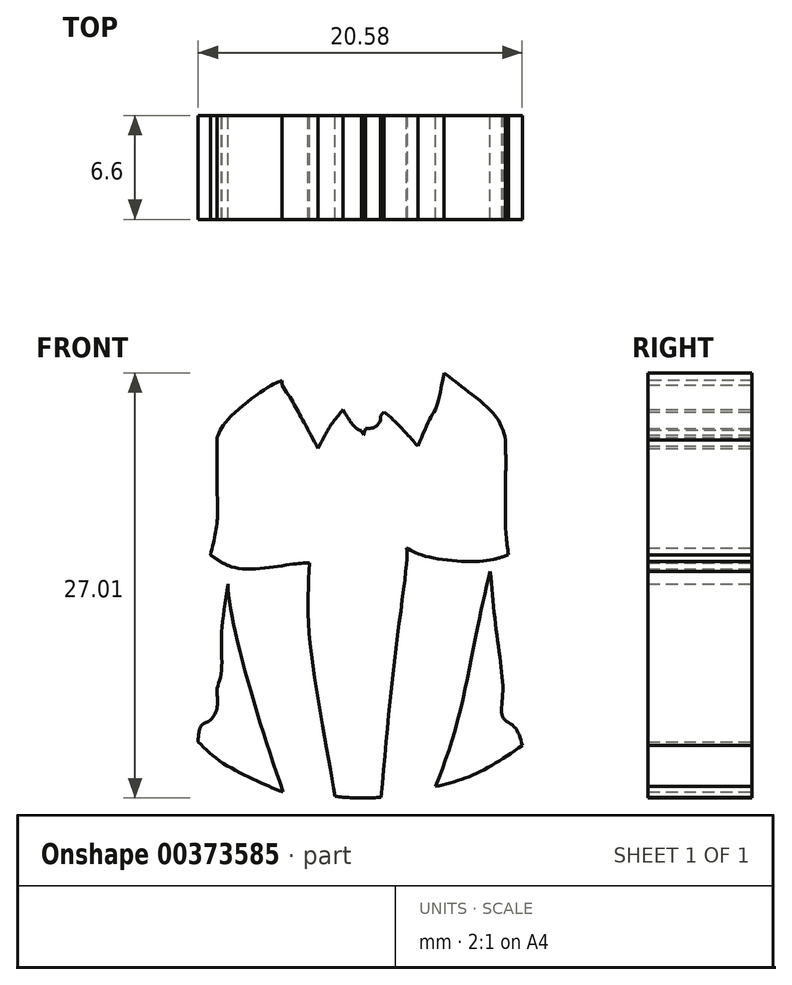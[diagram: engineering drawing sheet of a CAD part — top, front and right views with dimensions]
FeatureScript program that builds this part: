
annotation { "Feature Type Name" : "Feature", "Feature Type Description" : "" }
export const myFeature = defineFeature(function(context is Context, id is Id, definition is map)
    precondition{}
    {
        {
            var Q0;
            Q0=qCreatedBy(makeId("Front.planeOp"),FACE);
            var sketch = newSketch(context, id + "F0", { "sketchPlane" : qUnion([Q0])});
            skFitSpline(sketch, "E0", {"points": [v(-35.78, 54.46) * mm, v(-33.09, 59.85) * mm, v(-24.77, 66.06) * mm, v(-13.06, 67.81) * mm, v(-3.45, 65.7) * mm, v(-1.58, 65.82) * mm], "startDerivative": vector(10.86, 29.93) * mm, "endDerivative": vector(15.04, 3.36) * mm});
            skFitSpline(sketch, "E1", {"points": [v(-6.38, 64.18) * mm, v(-3.34, 64.3) * mm, v(-1.58, 65.82) * mm], "startDerivative": vector(6.22, -0.6) * mm, "endDerivative": vector(3.32, 3.98) * mm});
            skFitSpline(sketch, "E2", {"points": [v(-6.38, 64.18) * mm, v(-1.58, 62.66) * mm, v(2.4, 58.56) * mm, v(3.93, 55.63) * mm], "startDerivative": vector(14.2, -2.58) * mm, "endDerivative": vector(4.35, -9.84) * mm});
            skFitSpline(sketch, "E3", {"points": [v(3.93, 55.63) * mm, v(6.86, 54.23) * mm, v(8.96, 54.34) * mm], "startDerivative": vector(5.45, -3.31) * mm, "endDerivative": vector(4.6, 0.89) * mm});
            skFitSpline(sketch, "E4", {"points": [v(3.93, 54.21) * mm, v(5.68, 52.47) * mm, v(8.96, 54.34) * mm], "startDerivative": vector(3.48, -5.52) * mm, "endDerivative": vector(6.49, 5.4) * mm});
            skFitSpline(sketch, "E5", {"points": [v(5.68, 52.47) * mm, v(6.86, 48.72) * mm, v(6.86, 43.1) * mm, v(5.68, 41.7) * mm], "startDerivative": vector(3.82, -9.5) * mm, "endDerivative": vector(-5.74, -4.27) * mm});
            skFitSpline(sketch, "E6", {"points": [v(0, 51.42) * mm, v(1.35, 47.78) * mm, v(1.35, 45.1) * mm], "startDerivative": vector(3.15, -6.86) * mm, "endDerivative": vector(-0.56, -5.76) * mm});
            skFitSpline(sketch, "E7", {"points": [v(0, 51.42) * mm, v(3.93, 47.78) * mm, v(4.93, 43.33) * mm, v(5.68, 41.7) * mm], "startDerivative": vector(11.87, -7.83) * mm, "endDerivative": vector(3.7, -5.88) * mm});
            skFitSpline(sketch, "E8", {"points": [v(-7.7, 51.06) * mm, v(-5.13, 50.09) * mm, v(-0.67, 47.3) * mm, v(1.35, 45.1) * mm], "startDerivative": vector(8.03, -2.55) * mm, "endDerivative": vector(5.45, -7.1) * mm});
            skFitSpline(sketch, "E9", {"points": [v(-7.7, 51.06) * mm, v(-5.83, 48.77) * mm, v(-1.79, 45.96) * mm], "startDerivative": vector(3.67, -5.32) * mm, "endDerivative": vector(7.99, -4.9) * mm});
            skFitSpline(sketch, "E10", {"points": [v(-1.79, 45.96) * mm, v(-4.78, 45.96) * mm, v(-11.33, 49.25) * mm, v(-14.95, 51.76) * mm], "startDerivative": vector(-10.08, -1.7) * mm, "endDerivative": vector(-9.87, 7.2) * mm});
            skFitSpline(sketch, "E11", {"points": [v(-11.68, 45.1) * mm, v(-12.44, 48.14) * mm, v(-14.95, 51.76) * mm], "startDerivative": vector(-1, 6.65) * mm, "endDerivative": vector(-5.43, 6.69) * mm});
            skFitSpline(sketch, "E12", {"points": [v(-11.68, 45.1) * mm, v(-13.97, 47.7) * mm, v(-19.5, 51.76) * mm], "startDerivative": vector(-4.7, 6.12) * mm, "endDerivative": vector(-10.62, 7.16) * mm});
            skFitSpline(sketch, "E13", {"points": [v(-18.62, 45.1) * mm, v(-18.62, 48.14) * mm, v(-19.5, 51.76) * mm], "startDerivative": vector(0.4, 6.3) * mm, "endDerivative": vector(-2.13, 7.02) * mm});
            skFitSpline(sketch, "E14", {"points": [v(-20.14, 48.19) * mm, v(-19.3, 46.86) * mm, v(-18.62, 45.1) * mm], "startDerivative": vector(1.86, -2.65) * mm, "endDerivative": vector(1.2, -3.53) * mm});
            skFitSpline(sketch, "E15", {"points": [v(-22.6, 48.73) * mm, v(-20.78, 46.96) * mm, v(-19.55, 45.1) * mm], "startDerivative": vector(3.79, -3.33) * mm, "endDerivative": vector(2.3, -3.96) * mm});
            skFitSpline(sketch, "E16", {"points": [v(-20.14, 48.19) * mm, v(-19.3, 45.7) * mm, v(-19.55, 45.1) * mm], "startDerivative": vector(1.92, -4.36) * mm, "endDerivative": vector(-1.07, -1.52) * mm});
            skFitSpline(sketch, "E17", {"points": [v(-25.36, 50.22) * mm, v(-25.4, 46.4) * mm], "startDerivative": vector(-0.03, -3.81) * mm, "endDerivative": vector(-0.03, -3.81) * mm});
            skFitSpline(sketch, "E18", {"points": [v(-28.3, 48.16) * mm, v(-26.94, 47.5) * mm, v(-25.4, 46.4) * mm], "startDerivative": vector(2.87, -1.25) * mm, "endDerivative": vector(2.94, -2.24) * mm});
            skFitSpline(sketch, "E19", {"points": [v(-25.39, 47.04) * mm, v(-24.28, 48.16) * mm, v(-22.6, 48.73) * mm], "startDerivative": vector(2.06, 2.6) * mm, "endDerivative": vector(3.5, 0.8) * mm});
            skFitSpline(sketch, "E20", {"points": [v(-28.3, 48.16) * mm, v(-28.83, 43.89) * mm, v(-28.83, 43.03) * mm, v(-27.85, 38.2) * mm, v(-26.6, 36.06) * mm], "startDerivative": vector(-2.2, -17.32) * mm, "endDerivative": vector(5.7, -7.14) * mm});
            skFitSpline(sketch, "E21", {"points": [v(-28.3, 36.87) * mm, v(-27.46, 36.27) * mm, v(-26.6, 36.06) * mm], "startDerivative": vector(1.58, -1.34) * mm, "endDerivative": vector(1.82, -0.28) * mm});
            skFitSpline(sketch, "E22", {"points": [v(-30.88, 38.2) * mm, v(-29.25, 36.06) * mm, v(-27.37, 34.56) * mm], "startDerivative": vector(2.98, -4.44) * mm, "endDerivative": vector(4.04, -2.82) * mm});
            skFitSpline(sketch, "E23", {"points": [v(-28.3, 36.87) * mm, v(-27.85, 35.67) * mm, v(-27.37, 34.56) * mm], "startDerivative": vector(0.87, -2.39) * mm, "endDerivative": vector(0.98, -2.23) * mm});
            skFitSpline(sketch, "E24", {"points": [v(-30.88, 38.2) * mm, v(-30.28, 36.06) * mm, v(-28.3, 32.93) * mm], "startDerivative": vector(0.9, -4.76) * mm, "endDerivative": vector(4.12, -5.72) * mm});
            skFitSpline(sketch, "E25", {"points": [v(-30.88, 34.9) * mm, v(-29.77, 33.7) * mm, v(-28.3, 32.93) * mm], "startDerivative": vector(2.06, -2.62) * mm, "endDerivative": vector(3.1, -1.32) * mm});
            skFitSpline(sketch, "E26", {"points": [v(-30.88, 34.9) * mm, v(-30.26, 33.7) * mm, v(-29.1, 32.32) * mm], "startDerivative": vector(1.16, -2.58) * mm, "endDerivative": vector(2.37, -2.57) * mm});
            skFitSpline(sketch, "E27", {"points": [v(-31.59, 34.01) * mm, v(-30.54, 32.93) * mm, v(-29.1, 32.32) * mm], "startDerivative": vector(1.94, -2.42) * mm, "endDerivative": vector(3.02, -0.96) * mm});
            skFitSpline(sketch, "E28", {"points": [v(-31.59, 34.01) * mm, v(-30.88, 32.04) * mm, v(-29.47, 29.77) * mm, v(-27.85, 28.08) * mm], "startDerivative": vector(1.88, -6.17) * mm, "endDerivative": vector(5, -4.76) * mm});
            skFitSpline(sketch, "E29", {"points": [v(-32.7, 30.62) * mm, v(-31.27, 29.23) * mm, v(-29.1, 28.02) * mm, v(-27.85, 28.08) * mm], "startDerivative": vector(3.73, -4.02) * mm, "endDerivative": vector(4.29, 0.93) * mm});
            skFitSpline(sketch, "E30", {"points": [v(-32.7, 30.62) * mm, v(-33.17, 28.08) * mm, v(-32.15, 25.21) * mm, v(-29.1, 23.2) * mm, v(-27.37, 22.4) * mm], "startDerivative": vector(-2.96, -10.2) * mm, "endDerivative": vector(7.48, -3.45) * mm});
            skFitSpline(sketch, "E31", {"points": [v(-39.04, 37.32) * mm, v(-39.3, 32.93) * mm, v(-37.7, 28.98) * mm, v(-35.36, 26.2) * mm, v(-32.4, 23.59) * mm, v(-27.37, 22.4) * mm], "startDerivative": vector(-3.4, -21.75) * mm, "endDerivative": vector(24.84, -3.15) * mm});
            skFitSpline(sketch, "E32", {"points": [v(-39.04, 37.32) * mm, v(-39.93, 34.9) * mm, v(-41.09, 32.93) * mm], "startDerivative": vector(-1.58, -4.86) * mm, "endDerivative": vector(-2.54, -3.9) * mm});
            skFitSpline(sketch, "E33", {"points": [v(-35.78, 54.46) * mm, v(-39.04, 51.7) * mm, v(-41.02, 45.3) * mm, v(-41.02, 38.2) * mm, v(-41.09, 32.93) * mm], "startDerivative": vector(-16.55, -10.36) * mm, "endDerivative": vector(-0.72, -21.25) * mm});
            skFitSpline(sketch, "E34", {"points": [v(5.68, 41.7) * mm, v(6.42, 38.2) * mm, v(8.99, 34.9) * mm], "startDerivative": vector(0.72, -7.5) * mm, "endDerivative": vector(5.83, -6.1) * mm});
            skFitSpline(sketch, "E35", {"points": [v(8.99, 34.9) * mm, v(8.13, 34.01) * mm], "startDerivative": vector(-0.86, -0.89) * mm, "endDerivative": vector(-0.86, -0.89) * mm});
            skFitSpline(sketch, "E36", {"points": [v(-27.37, 22.4) * mm, v(-25.36, 20.57) * mm, v(-22.6, 19.8) * mm], "startDerivative": vector(3.73, -4.24) * mm, "endDerivative": vector(5.8, -0.97) * mm});
            skFitSpline(sketch, "E37", {"points": [v(-22.6, 19.8) * mm, v(-21.84, 21.8) * mm, v(-19.9, 24.77) * mm, v(-19.6, 23.8) * mm], "startDerivative": vector(1.48, 4.88) * mm, "endDerivative": vector(0.58, -6.35) * mm});
            skFitSpline(sketch, "E38", {"points": [v(-19.6, 23.8) * mm, v(-17.55, 26.1) * mm, v(-16.52, 25.98) * mm], "startDerivative": vector(3.39, 4.89) * mm, "endDerivative": vector(2.72, -1.06) * mm});
            skFitSpline(sketch, "E39", {"points": [v(-17.85, 23.8) * mm, v(-16.52, 25.98) * mm], "startDerivative": vector(1.33, 2.18) * mm, "endDerivative": vector(1.33, 2.18) * mm});
            skFitSpline(sketch, "E40", {"points": [v(-17.85, 23.8) * mm, v(-16.52, 24.3) * mm, v(-14.58, 24.3) * mm], "startDerivative": vector(2.72, 1.3) * mm, "endDerivative": vector(3.78, -0.29) * mm});
            skFitSpline(sketch, "E41", {"points": [v(-16.52, 22.4) * mm, v(-15.5, 23.24) * mm, v(-14.58, 24.3) * mm], "startDerivative": vector(2.13, 1.62) * mm, "endDerivative": vector(1.74, 2.17) * mm});
            skFitSpline(sketch, "E42", {"points": [v(-16.21, 20.46) * mm, v(-15.04, 21.35) * mm, v(-13.87, 22.8) * mm, v(-13.8, 23.8) * mm], "startDerivative": vector(3.34, 2.31) * mm, "endDerivative": vector(-0.34, 3.44) * mm});
            skFitSpline(sketch, "E43", {"points": [v(-16.52, 22.4) * mm, v(-15.73, 22.4) * mm, v(-14.58, 23.34) * mm, v(-14.38, 23.8) * mm, v(-13.8, 23.8) * mm], "startDerivative": vector(2.93, -0.64) * mm, "endDerivative": vector(3.34, -0.57) * mm});
            skFitSpline(sketch, "E44", {"points": [v(-19.6, 14.98) * mm, v(-18.89, 16.78) * mm, v(-16.52, 18.65) * mm, v(-14.58, 19.8) * mm, v(-14.58, 20.74) * mm, v(-16.21, 20.46) * mm], "startDerivative": vector(2.25, 9.04) * mm, "endDerivative": vector(-10.8, -4.04) * mm});
            skFitSpline(sketch, "E45", {"points": [v(-22.6, 19.8) * mm, v(-22.6, 18.51) * mm, v(-24.71, 14.98) * mm, v(-26.6, 12.03) * mm, v(-26.6, 10.16) * mm, v(-25.36, 7.7) * mm, v(-21.84, 8.1) * mm, v(-20.6, 12.48) * mm, v(-19.6, 14.98) * mm], "startDerivative": vector(2.63, -13.87) * mm, "endDerivative": vector(9.82, 18.02) * mm});
            skFitSpline(sketch, "E46", {"points": [v(-13.8, 37.83) * mm, v(-16.21, 38.2) * mm, v(-19.35, 38) * mm, v(-21.24, 37.1) * mm, v(-23.55, 35.39) * mm, v(-24.34, 34.01) * mm], "startDerivative": vector(-11.21, 2.22) * mm, "endDerivative": vector(-3.42, -8.47) * mm});
            skFitSpline(sketch, "E47", {"points": [v(-24.34, 34.01) * mm, v(-23.68, 33.33) * mm, v(-23.2, 32.93) * mm], "startDerivative": vector(1.23, -1.34) * mm, "endDerivative": vector(1.03, -0.8) * mm});
            skFitSpline(sketch, "E48", {"points": [v(-13.8, 37.83) * mm, v(-13.43, 37.6) * mm], "startDerivative": vector(0.37, -0.23) * mm, "endDerivative": vector(0.37, -0.23) * mm});
            skFitSpline(sketch, "E49", {"points": [v(-23.2, 32.93) * mm, v(-22.84, 33.82) * mm, v(-21.55, 35.3) * mm, v(-18.85, 36.72) * mm, v(-17.55, 37.26) * mm, v(-14.32, 37.51) * mm, v(-13.43, 37.6) * mm], "startDerivative": vector(2.32, 7) * mm, "endDerivative": vector(5.9, 0.82) * mm});
            skFitSpline(sketch, "E50", {"points": [v(-23.2, 32.93) * mm, v(-22.16, 32.07) * mm, v(-20.07, 31.13) * mm, v(-17.58, 31.02) * mm, v(-13.18, 32.93) * mm], "startDerivative": vector(5.1, -4.84) * mm, "endDerivative": vector(13.78, 7.2) * mm});
            skFitSpline(sketch, "E51", {"points": [v(-13.18, 32.93) * mm, v(-12.97, 34.38) * mm, v(-13.18, 36.06) * mm, v(-13.43, 37.05) * mm, v(-13.73, 37.56) * mm], "startDerivative": vector(1.07, 4.96) * mm, "endDerivative": vector(-1.82, 2.61) * mm});
            skFitSpline(sketch, "E52", {"points": [v(-16.59, 31.32) * mm, v(-17.53, 31.95) * mm, v(-18.37, 33.45) * mm, v(-18.45, 35.12) * mm, v(-17.58, 36.38) * mm, v(-16.01, 36.66) * mm, v(-14.94, 36.4) * mm, v(-14.2, 35.1) * mm, v(-14.22, 32.93) * mm, v(-14.33, 32.34) * mm], "startDerivative": vector(-9.83, 5) * mm, "endDerivative": vector(-1.64, -6.43) * mm});
            skFitSpline(sketch, "E53", {"points": [v(-17.58, 34.3) * mm, v(-17.55, 33.82) * mm, v(-17.21, 33.22) * mm, v(-16.8, 33.82) * mm, v(-16.46, 34.13) * mm, v(-16.42, 35.27) * mm, v(-16.8, 35.7) * mm, v(-17.55, 35.46) * mm, v(-17.79, 34.9) * mm, v(-17.75, 34.54) * mm, v(-17.58, 34.3) * mm]});
            skFitSpline(sketch, "E54", {"points": [v(-14.94, 34.22) * mm, v(-14.62, 34.17) * mm, v(-14.56, 33.22) * mm, v(-15, 33.22) * mm, v(-15.46, 33.22) * mm, v(-15.78, 33.22) * mm, v(-16, 33.45) * mm, v(-15.29, 33.53) * mm, v(-14.99, 33.82) * mm, v(-14.94, 34.22) * mm]});
            skFitSpline(sketch, "E55", {"points": [v(-21.86, 40.58) * mm, v(-20.54, 42) * mm, v(-19.37, 43) * mm, v(-17.81, 43.17) * mm, v(-17.4, 42.76) * mm, v(-17.79, 42.15) * mm, v(-19.19, 41.75) * mm, v(-20.51, 41.11) * mm, v(-21.86, 40.58) * mm]});
            skFitSpline(sketch, "E56", {"points": [v(-30.97, 28.2) * mm, v(-31.3, 28.04) * mm, v(-31.35, 27.36) * mm, v(-31.27, 26.59) * mm, v(-30.7, 25.8) * mm, v(-29.36, 25) * mm, v(-29.04, 24.94) * mm, v(-29.2, 25.39) * mm, v(-29.7, 25.86) * mm, v(-30.46, 26.52) * mm, v(-30.7, 26.9) * mm, v(-30.82, 27.76) * mm, v(-30.97, 28.2) * mm]});
            skFitSpline(sketch, "E57", {"points": [v(-28.79, 44.25) * mm, v(-27.31, 45.49) * mm, v(-25.77, 46.69) * mm], "startDerivative": vector(2.92, 2.5) * mm, "endDerivative": vector(3.1, 2.35) * mm});
            skFitSpline(sketch, "E58", {"points": [v(-23.28, 7.38) * mm, v(-23.34, 3.18) * mm, v(-22.86, 0) * mm, v(-22.26, -2.26) * mm, v(-22.26, -4.08) * mm, v(-21.65, -3.47) * mm, v(-20.8, -2.26) * mm], "startDerivative": vector(-0.82, -18.5) * mm, "endDerivative": vector(5.85, 8.57) * mm});
            skFitSpline(sketch, "E59", {"points": [v(-20.8, -2.26) * mm, v(-19.94, -4.93) * mm, v(-18.82, -7.88) * mm], "startDerivative": vector(1.69, -5.44) * mm, "endDerivative": vector(2.28, -5.8) * mm});
            skFitSpline(sketch, "E60", {"points": [v(-18.82, -7.88) * mm, v(-18.2, -6.6) * mm, v(-18, -5.44) * mm], "startDerivative": vector(1.37, 2.44) * mm, "endDerivative": vector(0.25, 2.45) * mm});
            skFitSpline(sketch, "E61", {"points": [v(-18, -5.44) * mm, v(-16.63, -7.12) * mm, v(-15.87, -7.32) * mm], "startDerivative": vector(2.26, -3.36) * mm, "endDerivative": vector(2, -0.14) * mm});
            skFitSpline(sketch, "E62", {"points": [v(-17.14, -1.42) * mm, v(-16.38, -3.5) * mm, v(-15.87, -7.32) * mm], "startDerivative": vector(1.96, -4.43) * mm, "endDerivative": vector(0.65, -7.25) * mm});
            skFitSpline(sketch, "E63", {"points": [v(-17.14, -1.42) * mm, v(-15.87, -2.06) * mm], "startDerivative": vector(1.27, -0.64) * mm, "endDerivative": vector(1.27, -0.64) * mm});
            skFitSpline(sketch, "E64", {"points": [v(-14.4, 8.3) * mm, v(-15.2, 6.36) * mm, v(-15.87, 3.77) * mm, v(-15.87, 0) * mm, v(-15.87, -2.06) * mm], "startDerivative": vector(-3.72, -8.42) * mm, "endDerivative": vector(-0.16, -8.38) * mm});
            skFitSpline(sketch, "E65", {"points": [v(-14.4, 8.3) * mm, v(-13.73, 6.87) * mm, v(-13.68, 3.62) * mm], "startDerivative": vector(1.93, -3.06) * mm, "endDerivative": vector(-0.36, -6.12) * mm});
            skFitSpline(sketch, "E66", {"points": [v(-9.36, 12.16) * mm, v(-9.97, 9.37) * mm, v(-11.09, 6.36) * mm, v(-13.68, 3.62) * mm], "startDerivative": vector(-1.82, -8.85) * mm, "endDerivative": vector(-8.2, -7.26) * mm});
            skFitSpline(sketch, "E67", {"points": [v(-9.36, 12.16) * mm, v(-8.44, 9.15) * mm, v(-6.35, 5.84) * mm, v(-5.23, 4.47) * mm], "startDerivative": vector(1.84, -8.43) * mm, "endDerivative": vector(3.88, -4.54) * mm});
            skFitSpline(sketch, "E68", {"points": [v(-5.23, 8.3) * mm, v(-5.23, 4.47) * mm], "startDerivative": vector(0, -3.83) * mm, "endDerivative": vector(0, -3.83) * mm});
            skFitSpline(sketch, "E69", {"points": [v(-5.23, 8.3) * mm, v(-2.64, 6.14) * mm, v(0, 4.47) * mm], "startDerivative": vector(5.02, -4.43) * mm, "endDerivative": vector(5.45, -3.23) * mm});
            skFitSpline(sketch, "E70", {"points": [v(-0.65, 6.2) * mm, v(0, 5.43) * mm, v(0, 4.47) * mm], "startDerivative": vector(1.62, -1.4) * mm, "endDerivative": vector(-0.32, -2.06) * mm});
            skFitSpline(sketch, "E71", {"points": [v(0, 5.43) * mm, v(0.87, 4.47) * mm, v(1.84, 2.89) * mm], "startDerivative": vector(1.94, -1.94) * mm, "endDerivative": vector(1.74, -3.11) * mm});
            skFitSpline(sketch, "E72", {"points": [v(0.77, 8.38) * mm, v(1.53, 6.6) * mm, v(1.94, 4.47) * mm, v(1.84, 2.89) * mm], "startDerivative": vector(2.45, -5.04) * mm, "endDerivative": vector(-0.63, -4.93) * mm});
            skFitSpline(sketch, "E73", {"points": [v(0.77, 8.38) * mm, v(3.16, 6.35) * mm, v(8.35, 3.5) * mm, v(10.23, 2.89) * mm], "startDerivative": vector(6.23, -6.11) * mm, "endDerivative": vector(6.35, -1.6) * mm});
            skFitSpline(sketch, "E74", {"points": [v(8.4, 5.43) * mm, v(9.47, 4.47) * mm, v(10.23, 2.89) * mm], "startDerivative": vector(2.43, -1.8) * mm, "endDerivative": vector(1.25, -3.26) * mm});
            skFitSpline(sketch, "E75", {"points": [v(9.47, 4.47) * mm, v(11.3, 3.17) * mm, v(14.43, 1.5) * mm, v(17.76, 0.9) * mm], "startDerivative": vector(5.9, -4.32) * mm, "endDerivative": vector(9.5, -0.91) * mm});
            skFitSpline(sketch, "E76", {"points": [v(17.76, 0.9) * mm, v(18.62, -1.15) * mm, v(18.96, -4.2) * mm, v(18.83, -4.8) * mm], "startDerivative": vector(2.57, -4.83) * mm, "endDerivative": vector(-0.84, -2.34) * mm});
            skFitSpline(sketch, "E77", {"points": [v(20.29, -1.88) * mm, v(20.25, -3.6) * mm, v(18.89, -4.64) * mm], "startDerivative": vector(0.57, -3.76) * mm, "endDerivative": vector(-3.37, -1.76) * mm});
            skFitSpline(sketch, "E78", {"points": [v(20.25, -3.6) * mm, v(19.66, -5.87) * mm, v(18.54, -8.86) * mm], "startDerivative": vector(-1.1, -4.78) * mm, "endDerivative": vector(-2.28, -5.73) * mm});
            skFitSpline(sketch, "E79", {"points": [v(18.54, -8.86) * mm, v(20.25, -7.54) * mm, v(21.54, -5.65) * mm], "startDerivative": vector(3.67, 2.44) * mm, "endDerivative": vector(2.32, 3.97) * mm});
            skFitSpline(sketch, "E80", {"points": [v(20.25, -8.86) * mm, v(21.11, -7.37) * mm, v(21.54, -5.65) * mm], "startDerivative": vector(1.96, 2.91) * mm, "endDerivative": vector(0.63, 3.5) * mm});
            skFitSpline(sketch, "E81", {"points": [v(20.25, -8.86) * mm, v(21.54, -7.7) * mm, v(22.57, -4.64) * mm], "startDerivative": vector(3.33, 2.19) * mm, "endDerivative": vector(1.4, 6.06) * mm});
            skFitSpline(sketch, "E82", {"points": [v(26.04, 4.47) * mm, v(25.9, 1.67) * mm, v(24.3, -2.57) * mm, v(22.57, -4.64) * mm], "startDerivative": vector(0.27, -8.4) * mm, "endDerivative": vector(-5.95, -5.77) * mm});
            skFitSpline(sketch, "E83", {"points": [v(20.25, 23.62) * mm, v(23.8, 18.8) * mm, v(26.54, 12.9) * mm, v(27.62, 7.28) * mm, v(26.04, 4.47) * mm], "startDerivative": vector(14.13, -17.43) * mm, "endDerivative": vector(-10.63, -12.77) * mm});
            skFitSpline(sketch, "E84", {"points": [v(10.72, 30.44) * mm, v(14.03, 28.92) * mm, v(20.25, 23.62) * mm], "startDerivative": vector(7.85, -2.76) * mm, "endDerivative": vector(10.99, -10.37) * mm});
            skFitSpline(sketch, "E85", {"points": [v(-18.43, -7.16) * mm, v(-17.63, -8.03) * mm, v(-16.42, -9) * mm], "startDerivative": vector(1.6, -1.88) * mm, "endDerivative": vector(2.41, -1.8) * mm});
            skFitSpline(sketch, "E86", {"points": [v(-16.42, -9) * mm, v(-16.15, -11.08) * mm, v(-15.76, -12.96) * mm, v(-14.27, -14.41) * mm], "startDerivative": vector(0.9, -6.15) * mm, "endDerivative": vector(5.24, -3.93) * mm});
            skFitSpline(sketch, "E87", {"points": [v(-14.27, -14.41) * mm, v(-8.74, -17.13) * mm, v(0.52, -18.6) * mm, v(10.03, -17.8) * mm, v(16.3, -15.35) * mm, v(18.33, -11.69) * mm, v(18.99, -9.75) * mm, v(20.25, -8.86) * mm], "startDerivative": vector(32.62, -19.16) * mm, "endDerivative": vector(18.52, 9.45) * mm});
            skFitSpline(sketch, "E88", {"points": [v(-4.09, -11.59) * mm, v(-3.93, -13.01) * mm, v(-1.75, -14.74) * mm, v(3.5, -14.95) * mm, v(6.4, -13.78) * mm, v(7.16, -12.5) * mm], "startDerivative": vector(-0.66, -9.66) * mm, "endDerivative": vector(3.65, 8.99) * mm});
            skFitSpline(sketch, "E89", {"points": [v(-4.09, -11.59) * mm, v(-1.75, -11.18) * mm, v(2.88, -11.13) * mm, v(6.34, -11.59) * mm, v(7.16, -12.5) * mm], "startDerivative": vector(9.19, 2.09) * mm, "endDerivative": vector(3.56, -6.23) * mm});
            skFitSpline(sketch, "E90", {"points": [v(-13.14, -2.74) * mm, v(-11.16, -1.46) * mm, v(-7.19, -1) * mm, v(-4.7, -1.87) * mm, v(-4.09, -3.2) * mm], "startDerivative": vector(7.11, 5.91) * mm, "endDerivative": vector(1.95, -7.59) * mm});
            skFitSpline(sketch, "E91", {"points": [v(-12.53, -3.9) * mm, v(-10.3, -2.69) * mm, v(-6.22, -2.58) * mm, v(-4.9, -3.6) * mm], "startDerivative": vector(5.8, 4.3) * mm, "endDerivative": vector(3.8, -4.53) * mm});
            skLineSegment(sketch, "E92", {"start": v(-13.14, -2.74) * mm, "end": v(-11.9, -2.74) * mm});
            skLineSegment(sketch, "E93", {"start": v(-11.9, -2.74) * mm, "end": v(-12.53, -3.9) * mm});
            skLineSegment(sketch, "E94", {"start": v(-4.9, -3.6) * mm, "end": v(-4.09, -3.2) * mm});
            skLineSegment(sketch, "E95", {"start": v(6.55, -2.23) * mm, "end": v(7.31, -3.2) * mm});
            skFitSpline(sketch, "E96", {"points": [v(6.55, -2.23) * mm, v(8.38, -1.16) * mm, v(9.6, -0.75) * mm, v(11.79, -0.65) * mm, v(15.15, -2.23) * mm], "startDerivative": vector(8, 5.03) * mm, "endDerivative": vector(10.7, -6.4) * mm});
            skFitSpline(sketch, "E97", {"points": [v(7.31, -3.2) * mm, v(8.74, -2.4) * mm, v(11.46, -2.07) * mm, v(14.47, -2.85) * mm, v(14.97, -3.2) * mm], "startDerivative": vector(5.6, 3.74) * mm, "endDerivative": vector(2.6, -2.24) * mm});
            skLineSegment(sketch, "E98", {"start": v(14.97, -3.2) * mm, "end": v(14.75, -2.5) * mm});
            skLineSegment(sketch, "E99", {"start": v(14.75, -2.5) * mm, "end": v(15.15, -2.23) * mm});
            skFitSpline(sketch, "E100", {"points": [v(-10.76, 3.1) * mm, v(-9.28, 4.27) * mm, v(-7.37, 4.73) * mm, v(-5.92, 4.45) * mm], "startDerivative": vector(3.94, 3.8) * mm, "endDerivative": vector(4.52, -1.34) * mm});
            skFitSpline(sketch, "E101", {"points": [v(-10.76, 3.1) * mm, v(-9.5, 3.3) * mm, v(-7.58, 3.56) * mm, v(-5.72, 3.53) * mm, v(-5.46, 4.12) * mm, v(-5.92, 4.45) * mm], "startDerivative": vector(5.75, 0.81) * mm, "endDerivative": vector(-4.31, 1.76) * mm});
            skFitSpline(sketch, "E102", {"points": [v(0.85, -8.55) * mm, v(1.9, -8.23) * mm, v(2.45, -7.68) * mm, v(2.9, -7.71) * mm, v(2.7, -8.55) * mm, v(0.85, -8.55) * mm]});
            skFitSpline(sketch, "E103", {"points": [v(-2.2, -18.44) * mm, v(-1.78, -19.48) * mm, v(0, -20.69) * mm, v(0.97, -21.23) * mm, v(1, -21.96) * mm, v(1.06, -23.14) * mm, v(1.3, -23.65) * mm], "startDerivative": vector(1.27, -6.3) * mm, "endDerivative": vector(2.3, -3.66) * mm});
            skFitSpline(sketch, "E104", {"points": [v(4.57, -18.5) * mm, v(4.57, -19.45) * mm, v(4.03, -20.42) * mm, v(2.27, -20.72) * mm, v(2.03, -21.63) * mm, v(2.03, -22.14) * mm, v(1.58, -22.93) * mm, v(1.3, -23.65) * mm], "startDerivative": vector(0.44, -6.45) * mm, "endDerivative": vector(-1.58, -5.57) * mm});
            skFitSpline(sketch, "E105", {"points": [v(2.05, -21.8) * mm, v(3.03, -22.55) * mm, v(4.74, -24.36) * mm], "startDerivative": vector(2.26, -1.57) * mm, "endDerivative": vector(3.07, -3.46) * mm});
            skFitSpline(sketch, "E106", {"points": [v(4.74, -24.36) * mm, v(5.52, -22.62) * mm, v(5.96, -21.76) * mm, v(6.3, -20.28) * mm, v(6.42, -19.7) * mm], "startDerivative": vector(2.6, 6.16) * mm, "endDerivative": vector(0.63, 2.75) * mm});
            skFitSpline(sketch, "E107", {"points": [v(4.74, -18.5) * mm, v(5.46, -18.87) * mm, v(6.42, -19.7) * mm], "startDerivative": vector(1.6, -0.7) * mm, "endDerivative": vector(1.74, -1.68) * mm});
            skFitSpline(sketch, "E108", {"points": [v(-1.58, -24.52) * mm, v(-0.83, -23.1) * mm, v(0, -22.03) * mm], "startDerivative": vector(1.38, 2.82) * mm, "endDerivative": vector(1.8, 2.13) * mm});
            skFitSpline(sketch, "E109", {"points": [v(0, -22.03) * mm, v(0.3, -22.55) * mm, v(0.87, -23.26) * mm, v(1.15, -23.38) * mm], "startDerivative": vector(0.72, -1.4) * mm, "endDerivative": vector(1.1, -0.25) * mm});
            skFitSpline(sketch, "E110", {"points": [v(1.43, -23.25) * mm, v(2.06, -23.12) * mm, v(2.38, -22.67) * mm, v(2.38, -22.47) * mm, v(2.6, -22.19) * mm], "startDerivative": vector(2.17, 0.05) * mm, "endDerivative": vector(1.29, 1.29) * mm});
            skFitSpline(sketch, "E111", {"points": [v(-4.86, 40.56) * mm, v(-3.95, 42.26) * mm, v(-0.8, 44.32) * mm, v(3.03, 44.62) * mm], "startDerivative": vector(2.4, 6.38) * mm, "endDerivative": vector(10.4, -0.42) * mm});
            skFitSpline(sketch, "E112", {"points": [v(-4.86, 40.56) * mm, v(-3.1, 41.6) * mm, v(-1.1, 42.86) * mm, v(2.6, 43.35) * mm], "startDerivative": vector(6.11, 3.24) * mm, "endDerivative": vector(10.26, 0.35) * mm});
            skFitSpline(sketch, "E113", {"points": [v(3.03, 44.62) * mm, v(3.5, 44.07) * mm, v(3.5, 41.9) * mm], "startDerivative": vector(1.5, -1.14) * mm, "endDerivative": vector(-0.4, -4.04) * mm});
            skFitSpline(sketch, "E114", {"points": [v(2.6, 43.35) * mm, v(3.5, 41.9) * mm], "startDerivative": vector(0.9, -1.45) * mm, "endDerivative": vector(0.9, -1.45) * mm});
            skFitSpline(sketch, "E115", {"points": [v(3.5, 41.9) * mm, v(3.5, 40.56) * mm, v(3.03, 39.25) * mm, v(1.35, 38.03) * mm, v(-1.32, 36.41) * mm], "startDerivative": vector(0.33, -6.36) * mm, "endDerivative": vector(-8.61, -5.3) * mm});
            skFitSpline(sketch, "E116", {"points": [v(-4.58, 40.71) * mm, v(-4.26, 39.7) * mm, v(-2.91, 37.42) * mm, v(-1.32, 36.41) * mm], "startDerivative": vector(0.9, -3.44) * mm, "endDerivative": vector(4.86, -2.15) * mm});
            skFitSpline(sketch, "E117", {"points": [v(1.21, 37.95) * mm, v(1.21, 38.84) * mm, v(1.06, 40.14) * mm, v(-0.32, 41.9) * mm, v(-2.2, 41.61) * mm, v(-3.11, 40.35) * mm, v(-2.88, 38.79) * mm, v(-2, 37.6) * mm, v(-0.65, 36.82) * mm], "startDerivative": vector(-0.04, 9.15) * mm, "endDerivative": vector(11.42, -5.53) * mm});
            skFitSpline(sketch, "E118", {"points": [v(-2.1, 40.9) * mm, v(-2.5, 40.56) * mm, v(-2.48, 39.94) * mm, v(-2.23, 39.74) * mm, v(-2.03, 39) * mm, v(-1.89, 38.6) * mm, v(-1.7, 38.86) * mm, v(-1.57, 39.3) * mm, v(-1.32, 39.31) * mm, v(-1.08, 39.92) * mm, v(-1.32, 40.88) * mm, v(-2.1, 40.9) * mm]});
            skFitSpline(sketch, "E119", {"points": [v(0.34, 39.56) * mm, v(0, 39.11) * mm, v(0.23, 38.86) * mm, v(0.38, 38.45) * mm, v(0.63, 38.54) * mm, v(0.74, 39.13) * mm, v(0.34, 39.56) * mm]});
            skFitSpline(sketch, "E120", {"points": [v(-2.2, -18.44) * mm, v(-3.13, -19.15) * mm, v(-3.83, -20.06) * mm, v(-3.9, -20.48) * mm], "startDerivative": vector(-2.44, -1.65) * mm, "endDerivative": vector(0.03, -1.67) * mm});
            skFitSpline(sketch, "E121", {"points": [v(-3.9, -20.48) * mm, v(-3.2, -21.57) * mm, v(-2.56, -22.72) * mm, v(-1.58, -24.52) * mm], "startDerivative": vector(2.36, -3.57) * mm, "endDerivative": vector(2.69, -4.92) * mm});
            skFitSpline(sketch, "E122", {"points": [v(-3.88, -20.21) * mm, v(-4.72, -20.6) * mm, v(-7.43, -22.8) * mm, v(-8, -23.82) * mm], "startDerivative": vector(-2.78, -0.96) * mm, "endDerivative": vector(-1.18, -3.3) * mm});
            skFitSpline(sketch, "E123", {"points": [v(-8, -23.82) * mm, v(-8, -27.3) * mm, v(-8, -29.13) * mm, v(-8.42, -31.26) * mm], "startDerivative": vector(-0.1, -9.5) * mm, "endDerivative": vector(-1.7, -7.06) * mm});
            skFitSpline(sketch, "E124", {"points": [v(-8.42, -31.26) * mm, v(-6.64, -32.13) * mm, v(-3.28, -31.87) * mm, v(-2.13, -31.77) * mm], "startDerivative": vector(4.64, -3.44) * mm, "endDerivative": vector(3.81, 0.18) * mm});
            skFitSpline(sketch, "E125", {"points": [v(3.74, -30.6) * mm, v(4.9, -31.26) * mm, v(8.78, -31.67) * mm, v(10.5, -31.26) * mm], "startDerivative": vector(3.44, -2.62) * mm, "endDerivative": vector(4.84, 1.76) * mm});
            skFitSpline(sketch, "E126", {"points": [v(6.42, -19.7) * mm, v(7.8, -20.79) * mm, v(9.74, -22.54) * mm, v(10.32, -23.97) * mm], "startDerivative": vector(3.98, -3.17) * mm, "endDerivative": vector(1.17, -4.82) * mm});
            skFitSpline(sketch, "E127", {"points": [v(10.32, -23.97) * mm, v(10.32, -26.7) * mm, v(10.32, -29.67) * mm, v(10.5, -31.26) * mm], "startDerivative": vector(0.05, -7.4) * mm, "endDerivative": vector(0.84, -5.33) * mm});
            skFitSpline(sketch, "E128", {"points": [v(13.83, -16.79) * mm, v(14.7, -21.7) * mm, v(15.07, -25.82) * mm, v(12.53, -26.67) * mm, v(10.32, -26.7) * mm], "startDerivative": vector(2.3, -15.84) * mm, "endDerivative": vector(-10.1, 0.17) * mm});
            skFitSpline(sketch, "E129", {"points": [v(-10.6, -16.4) * mm, v(-11.07, -21.47) * mm, v(-11.2, -26.7) * mm, v(-8, -27.3) * mm], "startDerivative": vector(-0.77, -13.29) * mm, "endDerivative": vector(13.92, 0.84) * mm});
            skFitSpline(sketch, "E130", {"points": [v(-2.13, -31.77) * mm, v(-2.13, -36.55) * mm, v(-0.86, -44.6) * mm, v(0, -48.5) * mm, v(0.96, -50.07) * mm], "startDerivative": vector(-0.95, -16.69) * mm, "endDerivative": vector(6.48, -8.72) * mm});
            skFitSpline(sketch, "E131", {"points": [v(-7.28, -31.96) * mm, v(-7.23, -34.16) * mm, v(-5.3, -41.85) * mm, v(-2.33, -50.5) * mm], "startDerivative": vector(-0.57, -9.22) * mm, "endDerivative": vector(7.34, -20.39) * mm});
            skFitSpline(sketch, "E132", {"points": [v(9.52, -31.56) * mm, v(8.57, -35.71) * mm, v(7.04, -42.63) * mm, v(4.9, -48.23) * mm], "startDerivative": vector(-3.26, -13.28) * mm, "endDerivative": vector(-6.75, -15.51) * mm});
            skFitSpline(sketch, "E133", {"points": [v(4.04, -30.83) * mm, v(4.04, -31.64) * mm, v(3.31, -37.55) * mm, v(2.3, -47.93) * mm], "startDerivative": vector(0.28, -4.57) * mm, "endDerivative": vector(-1.89, -21.56) * mm});
            skFitSpline(sketch, "E134", {"points": [v(13.72, -26.54) * mm, v(13.67, -29.99) * mm, v(13.73, -35.38) * mm, v(13.92, -40.15) * mm], "startDerivative": vector(-0.25, -11.06) * mm, "endDerivative": vector(0.61, -13.46) * mm});
            skFitSpline(sketch, "E135", {"points": [v(9.34, -32.31) * mm, v(9.82, -36.87) * mm, v(10.13, -40.15) * mm, v(10.13, -41.58) * mm, v(10.88, -42.2) * mm, v(11.37, -43.38) * mm], "startDerivative": vector(1.4, -15.85) * mm, "endDerivative": vector(2.14, -8.64) * mm});
            skFitSpline(sketch, "E136", {"points": [v(-7.32, -33.12) * mm, v(-7.71, -36.2) * mm, v(-7.71, -37.77) * mm, v(-7.8, -39.1) * mm, v(-8, -39.76) * mm, v(-8, -40.9) * mm, v(-8.49, -41.8) * mm, v(-9, -42.11) * mm, v(-9.21, -43.15) * mm], "startDerivative": vector(-2.64, -16.89) * mm, "endDerivative": vector(-0.53, -10.83) * mm});
            skFitSpline(sketch, "E137", {"points": [v(-9.21, -43.15) * mm, v(-7.79, -44.39) * mm, v(-5.55, -45.6) * mm, v(-3.81, -46.34) * mm], "startDerivative": vector(4.1, -4.02) * mm, "endDerivative": vector(5.4, -2.04) * mm});
            skFitSpline(sketch, "E138", {"points": [v(-0.5, -46.61) * mm, v(0.88, -46.72) * mm, v(2.4, -46.68) * mm], "startDerivative": vector(2.8, -0.29) * mm, "endDerivative": vector(3.04, 0.15) * mm});
            skFitSpline(sketch, "E139", {"points": [v(5.86, -46) * mm, v(8.42, -45.18) * mm, v(11.37, -43.38) * mm], "startDerivative": vector(5.45, 1.34) * mm, "endDerivative": vector(5.58, 3.83) * mm});
            skFitSpline(sketch, "E140", {"points": [v(13.92, -40.15) * mm, v(10.13, -40.15) * mm], "startDerivative": vector(-3.78, 0) * mm, "endDerivative": vector(-3.78, 0) * mm});
            skFitSpline(sketch, "E141", {"points": [v(13.92, -43.38) * mm, v(13.92, -40.15) * mm], "startDerivative": vector(0, 3.22) * mm, "endDerivative": vector(0, 3.22) * mm});
            skFitSpline(sketch, "E142", {"points": [v(11.37, -43.38) * mm, v(13.92, -43.38) * mm, v(18.25, -44.44) * mm, v(20.2, -46.46) * mm, v(20.62, -50.35) * mm, v(17, -52.54) * mm, v(10.75, -53.8) * mm, v(7.9, -54.12) * mm, v(4.9, -54.42) * mm], "startDerivative": vector(22.04, 1.3) * mm, "endDerivative": vector(-27.53, -2.77) * mm});
            skFitSpline(sketch, "E143", {"points": [v(4.9, -48.23) * mm, v(3.6, -50.27) * mm], "startDerivative": vector(-1.3, -2.05) * mm, "endDerivative": vector(-1.3, -2.05) * mm});
            skFitSpline(sketch, "E144", {"points": [v(2.3, -47.93) * mm, v(0.96, -50.07) * mm], "startDerivative": vector(-1.34, -2.14) * mm, "endDerivative": vector(-1.34, -2.14) * mm});
            skFitSpline(sketch, "E145", {"points": [v(3.6, -50.27) * mm, v(5.42, -48.46) * mm], "startDerivative": vector(1.82, 1.82) * mm, "endDerivative": vector(1.82, 1.82) * mm});
            skFitSpline(sketch, "E146", {"points": [v(5.42, -48.46) * mm, v(7.7, -48.06) * mm, v(10, -47.59) * mm, v(13.36, -45.61) * mm, v(17.63, -45.22) * mm, v(19.64, -46.8) * mm, v(20.03, -49.6) * mm, v(19.2, -50.87) * mm, v(18.09, -52.2) * mm], "startDerivative": vector(19.5, 3.85) * mm, "endDerivative": vector(-11.06, -13.53) * mm});
            skFitSpline(sketch, "E147", {"points": [v(-9.21, -43.15) * mm, v(-11.52, -42.73) * mm, v(-14.56, -42.73) * mm, v(-17.14, -43.15) * mm, v(-18.5, -44.68) * mm], "startDerivative": vector(-9.17, 2.14) * mm, "endDerivative": vector(-5.04, -8) * mm});
            skFitSpline(sketch, "E148", {"points": [v(-3.13, -50.5) * mm, v(-6.67, -48.46) * mm, v(-9.87, -46.86) * mm, v(-11.89, -45.97) * mm, v(-13.9, -44.42) * mm, v(-15.65, -43.9) * mm, v(-17.8, -44.42) * mm, v(-18.5, -44.68) * mm, v(-18.89, -45.97) * mm, v(-18.95, -47.93) * mm, v(-17.4, -50.27) * mm, v(-13.57, -52.11) * mm, v(-8.32, -54.33) * mm, v(-7.3, -54.89) * mm, v(-6.3, -55.22) * mm], "startDerivative": vector(-37.34, 22.1) * mm, "endDerivative": vector(22.17, -6.3) * mm});
            skFitSpline(sketch, "E149", {"points": [v(-3.13, -50.5) * mm, v(-4.12, -52.41) * mm, v(-6.3, -55.22) * mm], "startDerivative": vector(-1.91, -4.23) * mm, "endDerivative": vector(-4.33, -5.17) * mm});
            skFitSpline(sketch, "E150", {"points": [v(3.6, -50.27) * mm, v(4.4, -51.39) * mm, v(4.7, -53.63) * mm, v(4.3, -54.72) * mm, v(4.9, -54.42) * mm], "startDerivative": vector(3.34, -3.74) * mm, "endDerivative": vector(4.67, 2.99) * mm});
            skFitSpline(sketch, "E151", {"points": [v(-3.13, -50.5) * mm, v(-1.75, -51.98) * mm, v(-0.66, -53.04) * mm], "startDerivative": vector(2.65, -2.9) * mm, "endDerivative": vector(2.3, -2.17) * mm});
            skPoint(sketch, "E152.1.internal.snap0", {"position": v(-2.98, -64.76) * mm});
            skFitSpline(sketch, "E152", {"points": [v(-6.3, -55.22) * mm, v(-2.98, -57.07) * mm], "startDerivative": vector(3.32, -1.86) * mm, "endDerivative": vector(3.32, -1.86) * mm});
            skFitSpline(sketch, "E153", {"points": [v(-2.98, -57.07) * mm, v(-2.33, -56.05) * mm], "startDerivative": vector(0.65, 1.03) * mm, "endDerivative": vector(0.65, 1.03) * mm});
            skFitSpline(sketch, "E154", {"points": [v(-0.66, -53.04) * mm, v(-1.04, -53.75) * mm], "startDerivative": vector(-0.38, -0.7) * mm, "endDerivative": vector(-0.38, -0.7) * mm});
            skFitSpline(sketch, "E155", {"points": [v(-2.33, -56.05) * mm, v(-2.98, -55.66) * mm, v(-3.13, -54.89) * mm, v(-2.73, -54.25) * mm, v(-1.64, -53.92) * mm, v(-1.04, -53.75) * mm], "startDerivative": vector(-3.88, 1.48) * mm, "endDerivative": vector(3, 0.98) * mm});
            skFitSpline(sketch, "E156", {"points": [v(-2.33, -51.37) * mm, v(-0.44, -50.5) * mm, v(2.5, -50.27) * mm, v(3.6, -50.27) * mm], "startDerivative": vector(4.88, 2.98) * mm, "endDerivative": vector(3.74, 0) * mm});
            skFitSpline(sketch, "E157", {"points": [v(0.96, -50.07) * mm, v(0.96, -50.31) * mm], "startDerivative": vector(0, -0.24) * mm, "endDerivative": vector(0, -0.24) * mm});
            skFitSpline(sketch, "E158", {"points": [v(-0.66, -53.04) * mm, v(0.96, -53.75) * mm, v(3.6, -55.22) * mm, v(3.6, -58.14) * mm, v(1.76, -60.17) * mm, v(0, -60) * mm, v(-1.87, -58.44) * mm, v(-2.98, -57.07) * mm], "startDerivative": vector(11.36, -5.5) * mm, "endDerivative": vector(-8.07, 10.6) * mm});
            skFitSpline(sketch, "E159", {"points": [v(4.3, -54.72) * mm, v(3.1, -54.72) * mm], "startDerivative": vector(-1.2, 0) * mm, "endDerivative": vector(-1.2, 0) * mm});
            skFitSpline(sketch, "E160", {"points": [v(-9.87, -27.31) * mm, v(-9.64, -30.06) * mm, v(-9.32, -35.11) * mm, v(-9.2, -39.1) * mm, v(-9.2, -40.86) * mm, v(-8.78, -41.96) * mm], "startDerivative": vector(1.1, -12.59) * mm, "endDerivative": vector(3.94, -8.02) * mm});
            skFitSpline(sketch, "E161", {"points": [v(-9.21, -39.6) * mm, v(-8, -39.76) * mm], "startDerivative": vector(1.21, -0.17) * mm, "endDerivative": vector(1.21, -0.17) * mm});
            skFitSpline(sketch, "E162", {"points": [v(-6.76, 19.07) * mm, v(-7.3, 18.18) * mm, v(-9.2, 18.38) * mm, v(-9.32, 18.88) * mm, v(-9.87, 20.62) * mm, v(-8.78, 21.27) * mm, v(-8, 22.07) * mm, v(-7.3, 21.72) * mm, v(-7.3, 20.72) * mm, v(-6.76, 19.07) * mm]});
            skFitSpline(sketch, "E163", {"points": [v(-7.3, 21.72) * mm, v(-6.3, 22.22) * mm, v(-5.23, 21.72) * mm, v(-4.52, 20.67) * mm, v(-5.23, 19.52) * mm, v(-4.67, 18.88) * mm, v(-6.8, 18.65) * mm], "startDerivative": vector(6.38, 4.7) * mm, "endDerivative": vector(-15.2, -0.03) * mm});
            skFitSpline(sketch, "E164", {"points": [v(-4.9, 21.44) * mm, v(-3.87, 22.67) * mm, v(-2.33, 22.82) * mm, v(-1.04, 22.37) * mm, v(-1.04, 20.37) * mm, v(-1.75, 19.32) * mm, v(-2.98, 19.57) * mm, v(-3.97, 18.83) * mm, v(-4.67, 18.88) * mm], "startDerivative": vector(6.56, 10.96) * mm, "endDerivative": vector(-7.83, 2.8) * mm});
            skFitSpline(sketch, "E165", {"points": [v(-0.94, 20.8) * mm, v(0.96, 19.87) * mm, v(2.6, 20.37) * mm, v(3.6, 21.32) * mm, v(3.6, 22.87) * mm, v(4.3, 23.22) * mm, v(3.6, 24.62) * mm, v(2.6, 24.87) * mm, v(1.52, 24.91) * mm, v(1.52, 25.76) * mm, v(0.52, 25.66) * mm, v(-0.66, 24.07) * mm, v(-1.75, 22.75) * mm], "startDerivative": vector(18.42, -12.7) * mm, "endDerivative": vector(-12.24, -12.87) * mm});
            skFitSpline(sketch, "E166", {"points": [v(-9.32, 18.88) * mm, v(-9.95, 18.33) * mm, v(-11.52, 18.38) * mm, v(-11.52, 18.88) * mm, v(-12.45, 18.88) * mm, v(-12.3, 20.37) * mm, v(-12.45, 21.72) * mm, v(-11, 21.72) * mm, v(-9.95, 21.17) * mm, v(-9.32, 21.02) * mm], "startDerivative": vector(-4.1, -6.34) * mm, "endDerivative": vector(7.28, -1) * mm});
            skFitSpline(sketch, "E167", {"points": [v(-12.45, 19.54) * mm, v(-13.75, 18.88) * mm, v(-15, 19.39) * mm], "startDerivative": vector(-2.55, -1.92) * mm, "endDerivative": vector(-2.56, 1.63) * mm});
            skFitSpline(sketch, "E168", {"points": [v(-12.45, 21.72) * mm, v(-13.45, 22.37) * mm, v(-14.1, 22.37) * mm], "startDerivative": vector(-1.8, 1.46) * mm, "endDerivative": vector(-1.5, -0.24) * mm});
            skFitSpline(sketch, "E169", {"points": [v(3.6, 22.87) * mm, v(4.9, 22.37) * mm, v(5.95, 23.62) * mm, v(7.9, 24.12) * mm, v(6.86, 25.41) * mm, v(6.61, 26.41) * mm, v(5.42, 27.11) * mm, v(4.3, 26.91) * mm, v(2.6, 26.26) * mm, v(2.6, 24.87) * mm], "startDerivative": vector(13.83, -9.17) * mm, "endDerivative": vector(3.72, -14.8) * mm});
            skFitSpline(sketch, "E170", {"points": [v(7.33, 24.87) * mm, v(8.46, 25.26) * mm, v(7.9, 27.06) * mm, v(7.9, 28.06) * mm, v(7.06, 28.1) * mm, v(5.95, 28) * mm, v(5.42, 27.11) * mm], "startDerivative": vector(9.25, 0.85) * mm, "endDerivative": vector(-2.49, -7.07) * mm});
            skFitSpline(sketch, "E171", {"points": [v(8.15, 26.3) * mm, v(9.26, 26.16) * mm, v(10.5, 27.56) * mm, v(10.06, 28.56) * mm, v(10.1, 29.26) * mm, v(9.26, 29.76) * mm, v(8.46, 30.06) * mm, v(7.46, 29.7) * mm, v(6.76, 28.76) * mm, v(6.32, 28.1) * mm], "startDerivative": vector(8.92, -3.87) * mm, "endDerivative": vector(-4.58, -6.2) * mm});
            skFitSpline(sketch, "E172", {"points": [v(-13.8, 23.8) * mm, v(-12.93, 25.26) * mm, v(-14.03, 26.91) * mm, v(-14.56, 26.91) * mm, v(-14.73, 27.8) * mm, v(-16.27, 27.11) * mm, v(-16.85, 26.1) * mm], "startDerivative": vector(6.96, 6.62) * mm, "endDerivative": vector(-1.96, -6.05) * mm});
            skFitSpline(sketch, "E173", {"points": [v(-16.85, 25.43) * mm, v(-16.52, 25.25) * mm, v(-16.17, 24.33) * mm], "startDerivative": vector(0.93, -0.28) * mm, "endDerivative": vector(0.47, -1.8) * mm});
            skFitSpline(sketch, "E174", {"points": [v(-13.14, 25.98) * mm, v(-11.52, 26.55) * mm, v(-11.52, 28.47) * mm, v(-11.52, 29.5) * mm, v(-12.93, 29.38) * mm, v(-13.76, 29.63) * mm, v(-14.73, 27.8) * mm], "startDerivative": vector(11.52, 1.32) * mm, "endDerivative": vector(-4.72, -13.22) * mm});
            skFitSpline(sketch, "E175", {"points": [v(-11.42, 27.11) * mm, v(-9.87, 27.8) * mm, v(-9.87, 29.18) * mm, v(-10.89, 30.07) * mm, v(-11.05, 31.14) * mm, v(-13.27, 31.55) * mm, v(-13.76, 29.63) * mm], "startDerivative": vector(10.88, 2.35) * mm, "endDerivative": vector(0.53, -13.09) * mm});
            skLineSegment(sketch, "E176", {"start": v(4.04, -30.83) * mm, "end": v(4.04, -30.82) * mm});
            skLineSegment(sketch, "E177", {"start": v(-11.44, 31.44) * mm, "end": v(-10.43, 31.84) * mm});
            skLineSegment(sketch, "E178", {"start": v(-10.43, 31.84) * mm, "end": v(-9.62, 32.65) * mm});
            skLineSegment(sketch, "E179", {"start": v(-9.62, 32.65) * mm, "end": v(-8.93, 31.14) * mm});
            skLineSegment(sketch, "E180", {"start": v(-8.93, 31.14) * mm, "end": v(-7.6, 30.17) * mm});
            skLineSegment(sketch, "E181", {"start": v(-7.6, 30.17) * mm, "end": v(-8.2, 28.85) * mm});
            skLineSegment(sketch, "E182", {"start": v(-8.2, 28.85) * mm, "end": v(-9.66, 28.41) * mm});
            skPoint(sketch, "E183.5.internal.snap0", {"position": v(-9.27, 31.9) * mm});
            skFitSpline(sketch, "E183", {"points": [v(-9.27, 31.9) * mm, v(-8.97, 33.04) * mm, v(-7.65, 33.8) * mm, v(-7.3, 34.54) * mm, v(-6.15, 33.6) * mm, v(-6.06, 31.9) * mm, v(-6.88, 30.77) * mm, v(-7.6, 30.17) * mm], "startDerivative": vector(0.05, 9.48) * mm, "endDerivative": vector(-5.81, -4.4) * mm});
            skFitSpline(sketch, "E184", {"points": [v(-6.31, 31.42) * mm, v(-5.25, 30.73) * mm, v(-4.48, 31.24) * mm, v(-3.16, 31.24) * mm, v(-2.9, 33.04) * mm, v(-3.33, 34.5) * mm, v(-4.78, 34.2) * mm, v(-5.72, 35.05) * mm, v(-6.67, 34.24) * mm], "startDerivative": vector(9.51, -9.34) * mm, "endDerivative": vector(-8.3, -11.28) * mm});
            skFitSpline(sketch, "E185", {"points": [v(-3.02, 34.1) * mm, v(-2.34, 35.05) * mm, v(-0.42, 34.88) * mm, v(0.52, 34.5) * mm, v(0, 33.5) * mm, v(0.65, 32.44) * mm, v(-1.14, 31.76) * mm, v(-2.93, 31.57) * mm], "startDerivative": vector(3.8, 9.23) * mm, "endDerivative": vector(-9.74, -0.65) * mm});
            skFitSpline(sketch, "E186", {"points": [v(0, 32) * mm, v(0.6, 31.03) * mm, v(1.5, 31.33) * mm, v(1.6, 32.35) * mm, v(2.5, 33.55) * mm, v(1.68, 34.15) * mm, v(1.5, 35.1) * mm, v(0, 34.8) * mm], "startDerivative": vector(2.92, -8.97) * mm, "endDerivative": vector(-12.08, -4.77) * mm});
            skFitSpline(sketch, "E187", {"points": [v(7.88, 29.96) * mm, v(6.68, 30.17) * mm, v(6.51, 32.31) * mm, v(7.46, 32.1) * mm, v(8.13, 34.01) * mm, v(9.68, 32.78) * mm, v(11.18, 32.18) * mm, v(10.72, 30.44) * mm, v(10.1, 29.26) * mm], "startDerivative": vector(-12.44, -2.64) * mm, "endDerivative": vector(-4.85, -8.9) * mm});
            skFitSpline(sketch, "E188", {"points": [v(6.35, 31.16) * mm, v(4.5, 31.16) * mm, v(4.25, 32.1) * mm, v(3.13, 32.61) * mm, v(3.73, 34.01) * mm, v(3.99, 35.35) * mm, v(4.8, 34.88) * mm, v(5.74, 35.86) * mm, v(8.13, 34.01) * mm], "startDerivative": vector(-17.35, -3.37) * mm, "endDerivative": vector(15.34, -17.76) * mm});
            skFitSpline(sketch, "E189", {"points": [v(3.86, 32.31) * mm, v(3.4, 31.2) * mm, v(2.75, 31.63) * mm, v(1.5, 31.33) * mm], "startDerivative": vector(-1.13, -4.65) * mm, "endDerivative": vector(-3.69, -1.82) * mm});
            skFitSpline(sketch, "E190", {"points": [v(1.57, 34.7) * mm, v(2.53, 35.05) * mm, v(3, 34.4) * mm, v(3.99, 35.35) * mm], "startDerivative": vector(3.34, 2.23) * mm, "endDerivative": vector(2.97, 4.1) * mm});
            skFitSpline(sketch, "E191", {"points": [v(-3.93, -13.01) * mm, v(-0.7, -13.01) * mm, v(3.99, -13.01) * mm, v(6.98, -12.95) * mm], "startDerivative": vector(9.57, 0.01) * mm, "endDerivative": vector(9.1, 0.25) * mm});
            skFitSpline(sketch, "E192", {"points": [v(-4.09, -12.48) * mm, v(-2.92, -11.84) * mm, v(2.05, -11.59) * mm, v(6.68, -11.84) * mm], "startDerivative": vector(4.31, 3.46) * mm, "endDerivative": vector(11.2, -0.76) * mm});
            skFitSpline(sketch, "E193", {"points": [v(-2.33, -50.5) * mm, v(-1.97, -51.15) * mm], "startDerivative": vector(0.36, -0.65) * mm, "endDerivative": vector(0.36, -0.65) * mm});
            skLineSegment(sketch, "E194", {"start": v(-16.85, 26.1) * mm, "end": v(-16.85, 26.1) * mm});
            skLineSegment(sketch, "E195", {"start": v(18.89, -4.64) * mm, "end": v(18.88, -4.64) * mm});
            skSolve(sketch);
        }
        {
            var Q0;
            {var subQ15=sQuery(id+"F0.wireOp",EDGE,"E106");Q0=makeQuery(id+"F0.imprint","IMPRINT",FACE,{"disambiguationData":[TD([[makeQuery(id+"F0.imprint","IMPRINT",EDGE,{"derivedFrom":subQ15}),-1.0]])]});}
            var Q1;
            {var subQ3=sQuery(id+"F0.wireOp",EDGE,"E139");Q1=makeQuery(id+"F0.imprint","IMPRINT",FACE,{"disambiguationData":[TD([[makeQuery(id+"F0.imprint","IMPRINT",EDGE,{"derivedFrom":subQ3}),1.0]])]});}
            var Q2;
            {var subQ0=sQuery(id+"F0.wireOp",EDGE,"E137");Q2=makeQuery(id+"F0.imprint","IMPRINT",FACE,{"disambiguationData":[TD([[makeQuery(id+"F0.imprint","IMPRINT",EDGE,{"derivedFrom":subQ0}),1.0]])]});}
            extrude(context, id + "F1", {"entities" : qUnion([Q0, Q1, Q2]), "depth" : 6.6 * mm});
        }
    });
